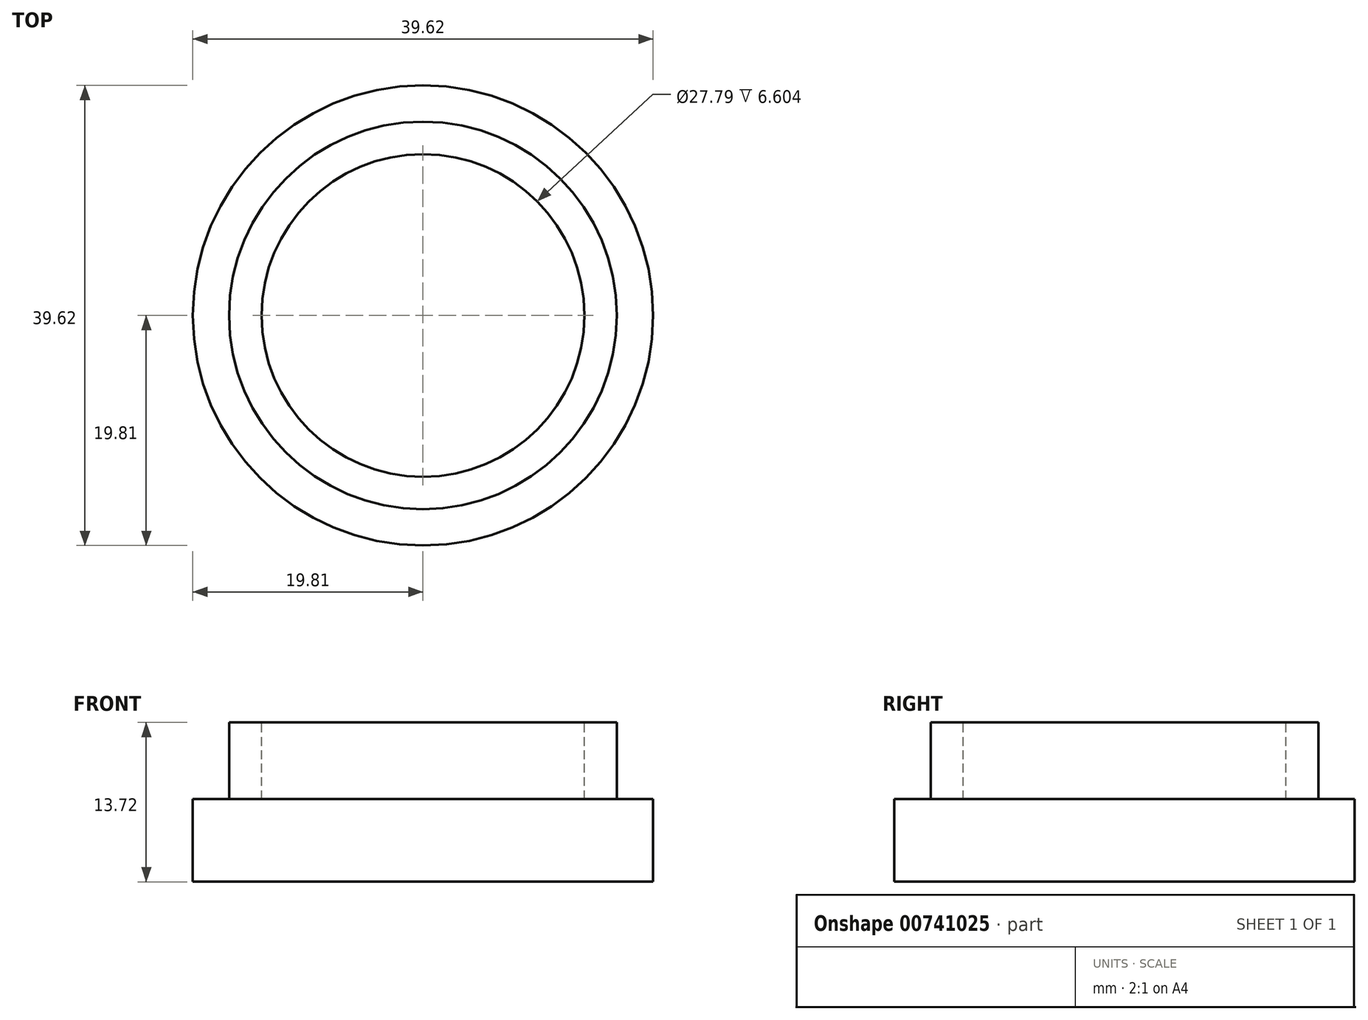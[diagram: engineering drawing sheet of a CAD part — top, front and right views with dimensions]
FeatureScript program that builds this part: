
annotation { "Feature Type Name" : "Feature", "Feature Type Description" : "" }
export const myFeature = defineFeature(function(context is Context, id is Id, definition is map)
    precondition{}
    {
        {
            var Q0;
            Q0=qCreatedBy(makeId("Front.planeOp"),FACE);
            var sketch = newSketch(context, id + "F0", { "sketchPlane" : qUnion([Q0])});
            skLineSegment(sketch, "E0.bottom", {"start": v(-19.81, 3.56) * mm, "end": v(19.81, 3.56) * mm});
            skLineSegment(sketch, "E0.top", {"start": v(-19.81, -3.56) * mm, "end": v(19.81, -3.56) * mm});
            skLineSegment(sketch, "E0.left", {"start": v(-19.81, 3.56) * mm, "end": v(-19.81, -3.56) * mm});
            skLineSegment(sketch, "E0.right", {"start": v(19.81, 3.56) * mm, "end": v(19.81, -3.56) * mm});
            skPoint(sketch, "E0.middle", {"position": v(0, 0) * mm});
            skPoint(sketch, "E1.middle", {"position": v(18.41, 6.86) * mm});
            skLineSegment(sketch, "E2", {"start": v(-16.69, 3.56) * mm, "end": v(-16.69, 10.16) * mm});
            skLineSegment(sketch, "E3", {"start": v(-16.69, 10.16) * mm, "end": v(-13.9, 10.16) * mm});
            skLineSegment(sketch, "E4", {"start": v(-13.9, 10.16) * mm, "end": v(-13.9, 3.56) * mm});
            skLineSegment(sketch, "E5", {"start": v(-13.9, 3.56) * mm, "end": v(-16.69, 3.56) * mm});
            skLineSegment(sketch, "E6", {"start": v(13.9, 3.56) * mm, "end": v(13.9, 10.16) * mm});
            skLineSegment(sketch, "E7", {"start": v(13.9, 10.16) * mm, "end": v(16.69, 10.16) * mm});
            skLineSegment(sketch, "E8", {"start": v(16.69, 10.16) * mm, "end": v(16.69, 3.56) * mm});
            skLineSegment(sketch, "E9", {"start": v(13.9, 3.56) * mm, "end": v(16.69, 3.56) * mm});
            skLineSegment(sketch, "E10", {"start": v(13.9, 3.56) * mm, "end": v(0, 3.56) * mm});
            skSolve(sketch);
        }
        {
            var Q0;
            Q0=qCreatedBy(makeId("Front.planeOp"),FACE);
            var sketch = newSketch(context, id + "F1", { "sketchPlane" : qUnion([Q0])});
            skLineSegment(sketch, "E11", {"start": v(0, 3.56) * mm, "end": v(0, -3.56) * mm});
            skLineSegment(sketch, "E12", {"start": v(0, 3.56) * mm, "end": v(19.81, 3.56) * mm});
            skLineSegment(sketch, "E13", {"start": v(19.81, 3.56) * mm, "end": v(19.81, -3.56) * mm});
            skLineSegment(sketch, "E14", {"start": v(19.81, -3.56) * mm, "end": v(0, -3.56) * mm});
            skSolve(sketch);
        }
        {
            var Q0;
            Q0 = qSketchRegion(id + "F1", true);
            var Q1;
            Q1=makeQuery(id+"F0.imprint","IMPRINT",FACE,{"disambiguationData":[TD([[makeQuery(id+"F0.imprint","IMPRINT",EDGE,{"derivedFrom":sQuery(id+"F0.wireOp",EDGE,"E6")}),-1.0]])]});
            var Q2;
            Q2=sQuery(id+"F1.wireOp",EDGE,"E11");
            revolve(context, id + "F2", {"surfaceOperationType" : NewSurfaceOperationType.NEW, "entities" : qUnion([Q0, Q1]), "axis" : qUnion([Q2]), "revolveType" : RevolveType.FULL});
        }
    });
